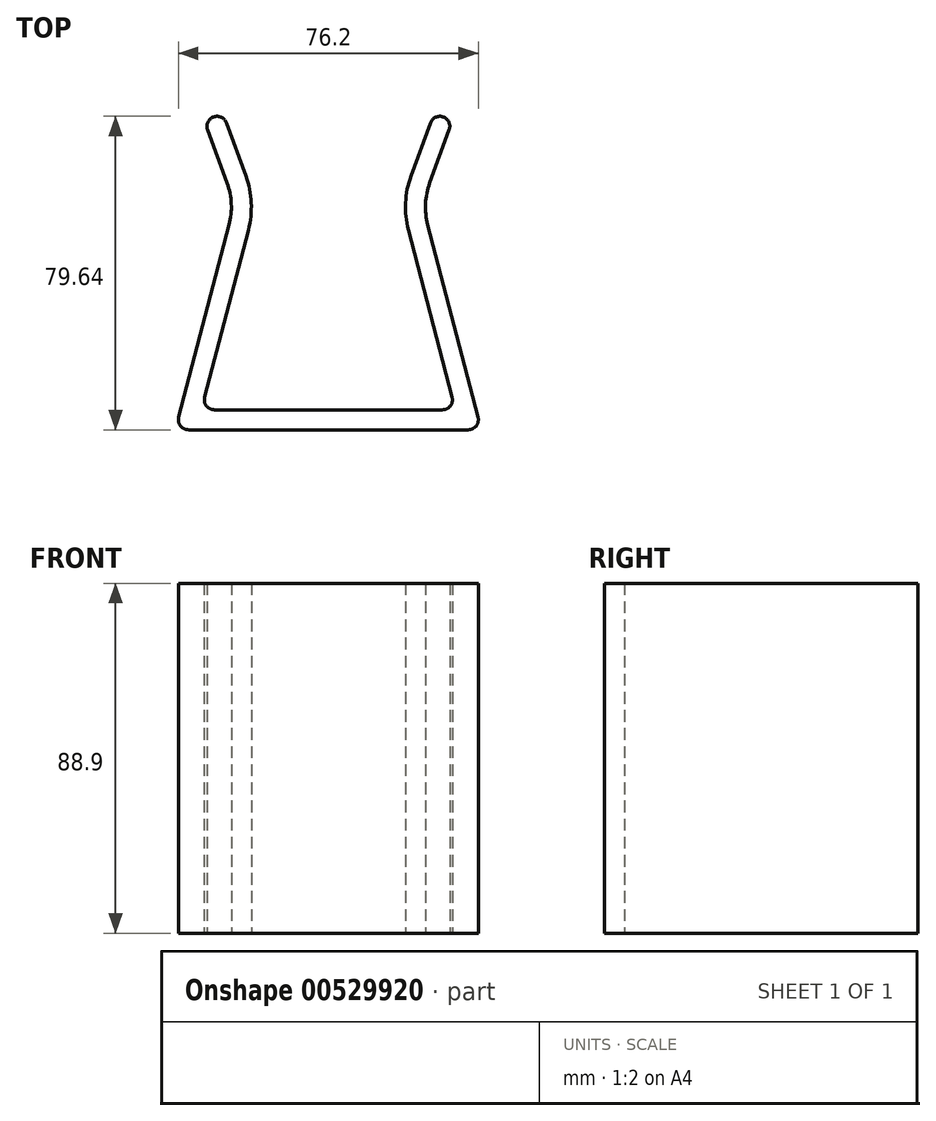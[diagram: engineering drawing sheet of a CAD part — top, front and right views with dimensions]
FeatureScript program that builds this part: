
annotation { "Feature Type Name" : "Feature", "Feature Type Description" : "" }
export const myFeature = defineFeature(function(context is Context, id is Id, definition is map)
    precondition{}
    {
        {
            var Q0;
            Q0=qCreatedBy(makeId("Top.planeOp"),FACE);
            var sketch = newSketch(context, id + "F0", { "sketchPlane" : qUnion([Q0])});
            skLineSegment(sketch, "E0", {"start": v(0, 0) * mm, "end": v(35.56, 0) * mm});
            skLineSegment(sketch, "E1.0", {"start": v(0, 5.08) * mm, "end": v(28.98, 5.08) * mm});
            skLineSegment(sketch, "E2.0", {"start": v(38.02, 3.18) * mm, "end": v(25.23, 52.08) * mm});
            skLineSegment(sketch, "E3", {"start": v(20.32, 50.8) * mm, "end": v(31.44, 8.26) * mm});
            skPoint(sketch, "E4.visualSharp", {"position": v(38.85, 0) * mm});
            skArc(sketch, "E4.filletArc", {"start": v(35.56, 0) * mm, "mid": v(37.57, 0.99) * mm, "end": v(38.02, 3.18) * mm});
            skPoint(sketch, "E5.visualSharp", {"position": v(32.27, 5.08) * mm});
            skArc(sketch, "E5.filletArc", {"start": v(28.98, 5.08) * mm, "mid": v(31, 6.07) * mm, "end": v(31.44, 8.26) * mm});
            skArc(sketch, "E6", {"start": v(20.97, 64.43) * mm, "mid": v(19.6, 57.66) * mm, "end": v(20.32, 50.8) * mm});
            skLineSegment(sketch, "E7", {"start": v(27.54, 23.18) * mm, "end": v(32.45, 24.47) * mm, "construction": true});
            skArc(sketch, "E8", {"start": v(25.74, 62.69) * mm, "mid": v(24.68, 57.42) * mm, "end": v(25.23, 52.08) * mm});
            skLineSegment(sketch, "E9", {"start": v(20.97, 64.43) * mm, "end": v(25.92, 77.97) * mm});
            skLineSegment(sketch, "E10", {"start": v(25.92, 77.97) * mm, "end": v(30.69, 76.23) * mm, "construction": true});
            skArc(sketch, "E11", {"start": v(30.69, 76.23) * mm, "mid": v(29.18, 79.49) * mm, "end": v(25.92, 77.97) * mm});
            skLineSegment(sketch, "E12", {"start": v(30.69, 76.23) * mm, "end": v(25.74, 62.69) * mm});
            skLineSegment(sketch, "E13.MirrorCS", {"start": v(-25.92, 77.97) * mm, "end": v(-30.69, 76.23) * mm, "construction": true});
            skArc(sketch, "E14.MirrorCS", {"start": v(-28.98, 5.08) * mm, "mid": v(-31, 6.07) * mm, "end": v(-31.44, 8.26) * mm});
            skArc(sketch, "E15.MirrorCS", {"start": v(-35.56, 0) * mm, "mid": v(-37.57, 0.99) * mm, "end": v(-38.02, 3.18) * mm});
            skArc(sketch, "E16.MirrorCS", {"start": v(-30.69, 76.23) * mm, "mid": v(-29.18, 79.49) * mm, "end": v(-25.92, 77.97) * mm});
            skLineSegment(sketch, "E17.MirrorCS", {"start": v(-27.54, 23.18) * mm, "end": v(-32.45, 24.47) * mm, "construction": true});
            skLineSegment(sketch, "E18.MirrorCS", {"start": v(0, 5.08) * mm, "end": v(-28.98, 5.08) * mm});
            skLineSegment(sketch, "E19.MirrorCS", {"start": v(-38.02, 3.18) * mm, "end": v(-25.23, 52.08) * mm});
            skLineSegment(sketch, "E20.MirrorCS", {"start": v(0, 0) * mm, "end": v(-35.56, 0) * mm});
            skLineSegment(sketch, "E21.MirrorCS", {"start": v(-20.32, 50.8) * mm, "end": v(-31.44, 8.26) * mm});
            skPoint(sketch, "E22.MirrorP", {"position": v(-38.85, 0) * mm});
            skPoint(sketch, "E23.MirrorP", {"position": v(-32.27, 5.08) * mm});
            skLineSegment(sketch, "E24.MirrorCS", {"start": v(-30.69, 76.23) * mm, "end": v(-25.74, 62.69) * mm});
            skLineSegment(sketch, "E25.MirrorCS", {"start": v(-20.97, 64.43) * mm, "end": v(-25.92, 77.97) * mm});
            skArc(sketch, "E26.MirrorCS", {"start": v(-25.74, 62.69) * mm, "mid": v(-24.68, 57.42) * mm, "end": v(-25.23, 52.08) * mm});
            skArc(sketch, "E27.MirrorCS", {"start": v(-20.97, 64.43) * mm, "mid": v(-19.6, 57.66) * mm, "end": v(-20.32, 50.8) * mm});
            skSolve(sketch);
        }
        {
            var Q0;
            Q0=makeQuery(id+"F0.imprint","IMPRINT",FACE,{"disambiguationData":[TD([[makeQuery(id+"F0.imprint","IMPRINT",EDGE,{"derivedFrom":sQuery(id+"F0.wireOp",EDGE,"E0")}),1.0]])]});
            extrude(context, id + "F1", {"entities" : qUnion([Q0]), "depth" : 88.9 * mm, "offsetDistance" : 25.4 * mm});
        }
    });
